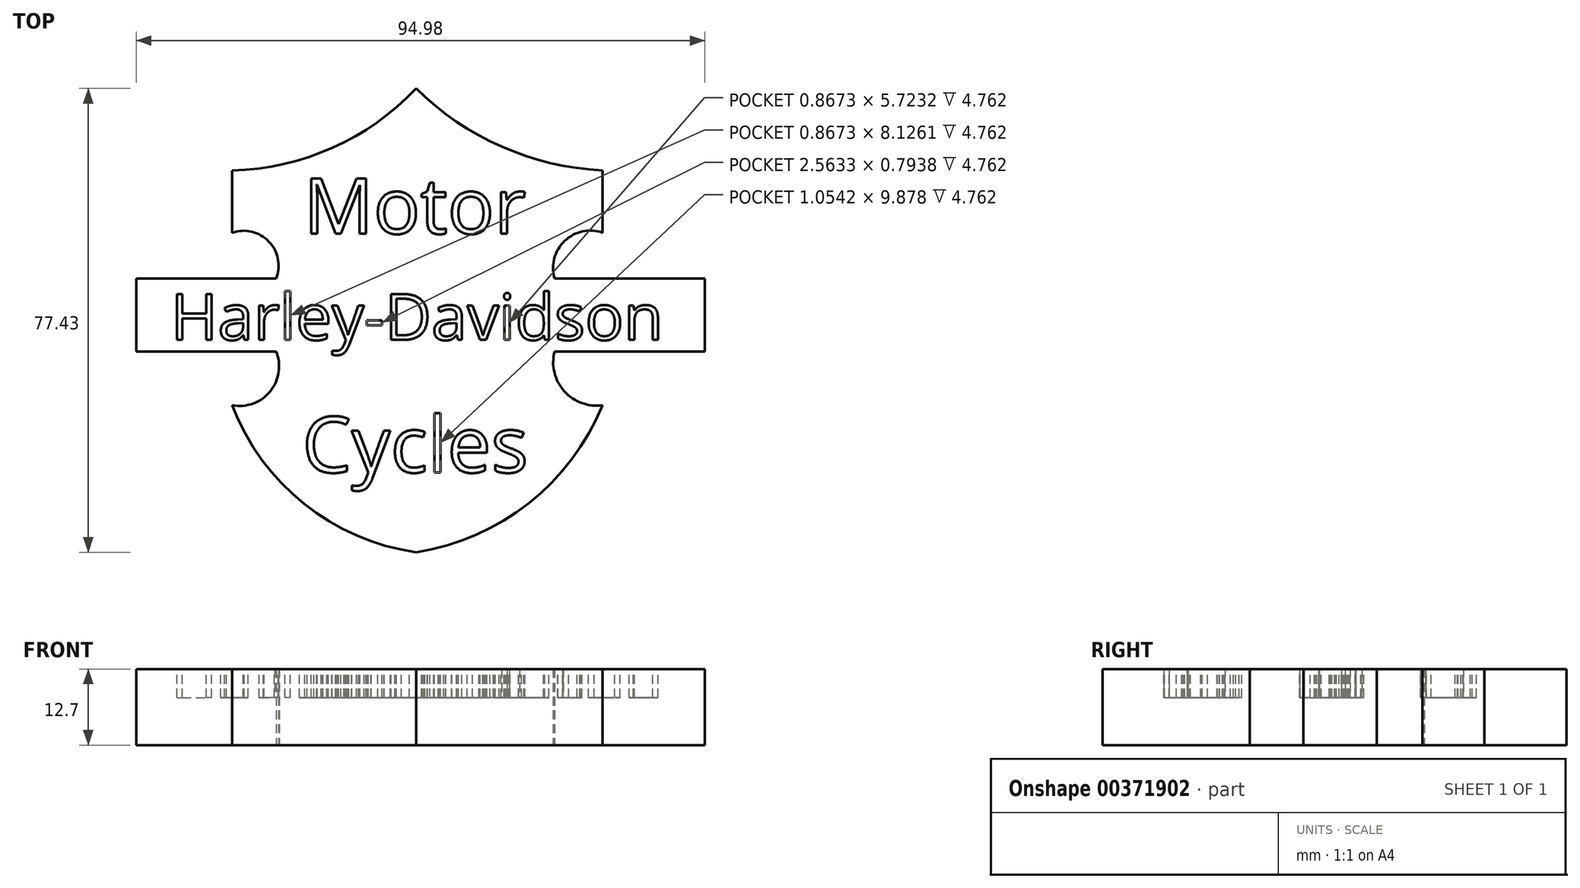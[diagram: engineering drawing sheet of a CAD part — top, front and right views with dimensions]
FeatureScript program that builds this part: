
annotation { "Feature Type Name" : "Feature", "Feature Type Description" : "" }
export const myFeature = defineFeature(function(context is Context, id is Id, definition is map)
    precondition{}
    {
        {
            var Q0;
            Q0=qCreatedBy(makeId("Top.planeOp"),FACE);
            var sketch = newSketch(context, id + "F0", { "sketchPlane" : qUnion([Q0])});
            skArc(sketch, "E0", {"start": v(-30.69, 35.65) * mm, "mid": v(-13.97, 39.42) * mm, "end": v(0, 49.34) * mm});
            skArc(sketch, "E1", {"start": v(0, 49.34) * mm, "mid": v(14.32, 39.61) * mm, "end": v(31.16, 35.65) * mm});
            skLineSegment(sketch, "E2", {"start": v(-30.69, 35.65) * mm, "end": v(-30.69, 25.26) * mm});
            skLineSegment(sketch, "E3", {"start": v(31.16, 35.65) * mm, "end": v(31.16, 25.26) * mm});
            skArc(sketch, "E4", {"start": v(31.16, 25.26) * mm, "mid": v(24.82, 23.9) * mm, "end": v(23.14, 17.63) * mm});
            skLineSegment(sketch, "E5", {"start": v(23.14, 17.63) * mm, "end": v(48.24, 17.63) * mm});
            skLineSegment(sketch, "E6", {"start": v(48.24, 17.63) * mm, "end": v(48.24, 5.43) * mm});
            skLineSegment(sketch, "E7", {"start": v(-46.74, 5.43) * mm, "end": v(-46.74, 17.63) * mm});
            skArc(sketch, "E8", {"start": v(23.14, 5.43) * mm, "mid": v(24.75, -1.2) * mm, "end": v(31.16, -3.54) * mm});
            skArc(sketch, "E9", {"start": v(-30.69, -3.54) * mm, "mid": v(-18.7, -20) * mm, "end": v(0, -28.1) * mm});
            skArc(sketch, "E10", {"start": v(0, -28.1) * mm, "mid": v(18.8, -19.9) * mm, "end": v(31.16, -3.54) * mm});
            skArc(sketch, "E11", {"start": v(-30.69, -3.54) * mm, "mid": v(-24.36, -1.24) * mm, "end": v(-23.35, 5.43) * mm});
            skArc(sketch, "E12", {"start": v(-23.35, 17.63) * mm, "mid": v(-24.58, 23.79) * mm, "end": v(-30.69, 25.26) * mm});
            skLineSegment(sketch, "E13", {"start": v(-23.35, 17.63) * mm, "end": v(-46.74, 17.63) * mm});
            skLineSegment(sketch, "E14", {"start": v(-46.74, 5.43) * mm, "end": v(-23.35, 5.43) * mm});
            skLineSegment(sketch, "E15", {"start": v(23.14, 5.43) * mm, "end": v(48.24, 5.43) * mm});
            skSolve(sketch);
        }
        {
            var Q0;
            Q0=makeQuery(id+"F0.imprint","IMPRINT",FACE,{"disambiguationData":[TD([[makeQuery(id+"F0.imprint","IMPRINT",EDGE,{"derivedFrom":sQuery(id+"F0.wireOp",EDGE,"E0")}),-1.0]])]});
            var Q1;
            Q1=makeQuery(id+"F0.imprint","IMPRINT",FACE,{"disambiguationData":[TD([[makeQuery(id+"F0.imprint","IMPRINT",EDGE,{"derivedFrom":sQuery(id+"F0.wireOp",EDGE,"38d3032f-426a-4906-8454-d546ac383862.sketch_text.stroke-173")}),1.0]])]});
            var Q2;
            Q2=makeQuery(id+"F0.imprint","IMPRINT",FACE,{"disambiguationData":[TD([[makeQuery(id+"F0.imprint","IMPRINT",EDGE,{"derivedFrom":sQuery(id+"F0.wireOp",EDGE,"38d3032f-426a-4906-8454-d546ac383862.sketch_text.stroke-216")}),1.0]])]});
            var Q3;
            Q3=makeQuery(id+"F0.imprint","IMPRINT",FACE,{"disambiguationData":[TD([[makeQuery(id+"F0.imprint","IMPRINT",EDGE,{"derivedFrom":sQuery(id+"F0.wireOp",EDGE,"fb05afc6-232a-44e7-864e-b6d0d33b0555.sketch_text.stroke-63")}),1.0]])]});
            var Q4;
            Q4=makeQuery(id+"F0.imprint","IMPRINT",FACE,{"disambiguationData":[TD([[makeQuery(id+"F0.imprint","IMPRINT",EDGE,{"derivedFrom":sQuery(id+"F0.wireOp",EDGE,"fb05afc6-232a-44e7-864e-b6d0d33b0555.sketch_text.stroke-27")}),1.0]])]});
            var Q5;
            Q5=makeQuery(id+"F0.imprint","IMPRINT",FACE,{"disambiguationData":[TD([[makeQuery(id+"F0.imprint","IMPRINT",EDGE,{"derivedFrom":sQuery(id+"F0.wireOp",EDGE,"38d3032f-426a-4906-8454-d546ac383862.sketch_text.stroke-102")}),1.0]])]});
            var Q6;
            Q6=makeQuery(id+"F0.imprint","IMPRINT",FACE,{"disambiguationData":[TD([[makeQuery(id+"F0.imprint","IMPRINT",EDGE,{"derivedFrom":sQuery(id+"F0.wireOp",EDGE,"38d3032f-426a-4906-8454-d546ac383862.sketch_text.stroke-31")}),1.0]])]});
            var Q7;
            Q7=makeQuery(id+"F0.imprint","IMPRINT",FACE,{"disambiguationData":[TD([[makeQuery(id+"F0.imprint","IMPRINT",EDGE,{"derivedFrom":sQuery(id+"F0.wireOp",EDGE,"38d3032f-426a-4906-8454-d546ac383862.sketch_text.stroke-70")}),1.0]])]});
            var Q8;
            Q8=makeQuery(id+"F0.imprint","IMPRINT",FACE,{"disambiguationData":[TD([[makeQuery(id+"F0.imprint","IMPRINT",EDGE,{"derivedFrom":sQuery(id+"F0.wireOp",EDGE,"38d3032f-426a-4906-8454-d546ac383862.sketch_text.stroke-128")}),1.0]])]});
            var Q9;
            Q9=makeQuery(id+"F0.imprint","IMPRINT",FACE,{"disambiguationData":[TD([[makeQuery(id+"F0.imprint","IMPRINT",EDGE,{"derivedFrom":sQuery(id+"F0.wireOp",EDGE,"3be71efd-9f48-4feb-90e3-6328f18f5e6b.sketch_text.stroke-64")}),1.0]])]});
            extrude(context, id + "F1", {"entities" : qUnion([Q0, Q1, Q2, Q3, Q4, Q5, Q6, Q7, Q8, Q9]), "depth" : 12.7 * mm});
        }
        {
            var Q0;
            Q0=makeQuery(id+"F1.opExtrude","CAP_FACE",FACE,{"disambiguationData":[OSD([sQuery(id+"F0.wireOp",EDGE,"E0"),sQuery(id+"F0.wireOp",EDGE,"E1"),sQuery(id+"F0.wireOp",EDGE,"E2"),sQuery(id+"F0.wireOp",EDGE,"E3"),sQuery(id+"F0.wireOp",EDGE,"E4"),sQuery(id+"F0.wireOp",EDGE,"E5"),sQuery(id+"F0.wireOp",EDGE,"E6"),sQuery(id+"F0.wireOp",EDGE,"E7"),sQuery(id+"F0.wireOp",EDGE,"E8"),sQuery(id+"F0.wireOp",EDGE,"E9"),sQuery(id+"F0.wireOp",EDGE,"E10"),sQuery(id+"F0.wireOp",EDGE,"E11"),sQuery(id+"F0.wireOp",EDGE,"E12"),sQuery(id+"F0.wireOp",EDGE,"E13"),sQuery(id+"F0.wireOp",EDGE,"E14"),sQuery(id+"F0.wireOp",EDGE,"E15")])],"isStart":false});
            var sketch = newSketch(context, id + "F2", { "sketchPlane" : qUnion([Q0])});
            skText(sketch, "E16", { "text": "Harley-Davidson", "fontName": "OpenSans-Regular.ttf"});
            skText(sketch, "E17", { "text": "Cycles", "fontName": "OpenSans-Regular.ttf"});
            skText(sketch, "E18", { "text": "Motor", "fontName": "OpenSans-Regular.ttf"});
            const initialGuessF2  = {"E16": [-0.04098, 0.00736, 1, 0, 0.0077], "E17": [-0.019, -0.01476, 1, 0, 0.00936], "E18": [-0.01876, 0.0251, 1, 0, 0.0093]};
            skSetInitialGuess(sketch, initialGuessF2);
            skSolve(sketch);
        }
        {
            var Q0;
            Q0=makeQuery(id+"F2.imprint","IMPRINT",FACE,{"disambiguationData":[TD([[makeQuery(id+"F2.imprint","IMPRINT",EDGE,{"derivedFrom":sQuery(id+"F2.wireOp",EDGE,"E16.sketch_text.stroke-224")}),-1.0]])]});
            var Q1;
            Q1=makeQuery(id+"F2.imprint","IMPRINT",FACE,{"disambiguationData":[TD([[makeQuery(id+"F2.imprint","IMPRINT",EDGE,{"derivedFrom":sQuery(id+"F2.wireOp",EDGE,"E16.sketch_text.stroke-207")}),-1.0]])]});
            var Q2;
            Q2=makeQuery(id+"F2.imprint","IMPRINT",FACE,{"disambiguationData":[TD([[makeQuery(id+"F2.imprint","IMPRINT",EDGE,{"derivedFrom":sQuery(id+"F2.wireOp",EDGE,"E16.sketch_text.stroke-182")}),-1.0]])]});
            var Q3;
            Q3=makeQuery(id+"F2.imprint","IMPRINT",FACE,{"disambiguationData":[TD([[makeQuery(id+"F2.imprint","IMPRINT",EDGE,{"derivedFrom":sQuery(id+"F2.wireOp",EDGE,"E16.sketch_text.stroke-158")}),-1.0]])]});
            var Q4;
            Q4=makeQuery(id+"F2.imprint","IMPRINT",FACE,{"disambiguationData":[TD([[makeQuery(id+"F2.imprint","IMPRINT",EDGE,{"derivedFrom":sQuery(id+"F2.wireOp",EDGE,"E16.sketch_text.stroke-146")}),-1.0]])]});
            var Q5;
            Q5=makeQuery(id+"F2.imprint","IMPRINT",FACE,{"disambiguationData":[TD([[makeQuery(id+"F2.imprint","IMPRINT",EDGE,{"derivedFrom":sQuery(id+"F2.wireOp",EDGE,"E16.sketch_text.stroke-150")}),-1.0]])]});
            var Q6;
            Q6=makeQuery(id+"F2.imprint","IMPRINT",FACE,{"disambiguationData":[TD([[makeQuery(id+"F2.imprint","IMPRINT",EDGE,{"derivedFrom":sQuery(id+"F2.wireOp",EDGE,"E16.sketch_text.stroke-136")}),-1.0]])]});
            var Q7;
            Q7=makeQuery(id+"F2.imprint","IMPRINT",FACE,{"disambiguationData":[TD([[makeQuery(id+"F2.imprint","IMPRINT",EDGE,{"derivedFrom":sQuery(id+"F2.wireOp",EDGE,"E16.sketch_text.stroke-109")}),-1.0]])]});
            var Q8;
            Q8=makeQuery(id+"F2.imprint","IMPRINT",FACE,{"disambiguationData":[TD([[makeQuery(id+"F2.imprint","IMPRINT",EDGE,{"derivedFrom":sQuery(id+"F2.wireOp",EDGE,"E16.sketch_text.stroke-95")}),-1.0]])]});
            var Q9;
            Q9=makeQuery(id+"F2.imprint","IMPRINT",FACE,{"disambiguationData":[TD([[makeQuery(id+"F2.imprint","IMPRINT",EDGE,{"derivedFrom":sQuery(id+"F2.wireOp",EDGE,"E16.sketch_text.stroke-91")}),-1.0]])]});
            var Q10;
            Q10=makeQuery(id+"F2.imprint","IMPRINT",FACE,{"disambiguationData":[TD([[makeQuery(id+"F2.imprint","IMPRINT",EDGE,{"derivedFrom":sQuery(id+"F2.wireOp",EDGE,"E16.sketch_text.stroke-75")}),-1.0]])]});
            var Q11;
            Q11=makeQuery(id+"F2.imprint","IMPRINT",FACE,{"disambiguationData":[TD([[makeQuery(id+"F2.imprint","IMPRINT",EDGE,{"derivedFrom":sQuery(id+"F2.wireOp",EDGE,"E16.sketch_text.stroke-56")}),-1.0]])]});
            var Q12;
            Q12=makeQuery(id+"F2.imprint","IMPRINT",FACE,{"disambiguationData":[TD([[makeQuery(id+"F2.imprint","IMPRINT",EDGE,{"derivedFrom":sQuery(id+"F2.wireOp",EDGE,"E16.sketch_text.stroke-52")}),-1.0]])]});
            var Q13;
            Q13=makeQuery(id+"F2.imprint","IMPRINT",FACE,{"disambiguationData":[TD([[makeQuery(id+"F2.imprint","IMPRINT",EDGE,{"derivedFrom":sQuery(id+"F2.wireOp",EDGE,"E16.sketch_text.stroke-39")}),-1.0]])]});
            var Q14;
            Q14=makeQuery(id+"F2.imprint","IMPRINT",FACE,{"disambiguationData":[TD([[makeQuery(id+"F2.imprint","IMPRINT",EDGE,{"derivedFrom":sQuery(id+"F2.wireOp",EDGE,"E16.sketch_text.stroke-12")}),-1.0]])]});
            var Q15;
            Q15=makeQuery(id+"F2.imprint","IMPRINT",FACE,{"disambiguationData":[TD([[makeQuery(id+"F2.imprint","IMPRINT",EDGE,{"derivedFrom":sQuery(id+"F2.wireOp",EDGE,"E16.sketch_text.stroke-0")}),-1.0]])]});
            var Q16;
            Q16=makeQuery(id+"F2.imprint","IMPRINT",FACE,{"disambiguationData":[TD([[makeQuery(id+"F2.imprint","IMPRINT",EDGE,{"derivedFrom":sQuery(id+"F2.wireOp",EDGE,"E18.sketch_text.stroke-0")}),-1.0]])]});
            var Q17;
            Q17=makeQuery(id+"F2.imprint","IMPRINT",FACE,{"disambiguationData":[TD([[makeQuery(id+"F2.imprint","IMPRINT",EDGE,{"derivedFrom":sQuery(id+"F2.wireOp",EDGE,"E18.sketch_text.stroke-18")}),-1.0]])]});
            var Q18;
            Q18=makeQuery(id+"F2.imprint","IMPRINT",FACE,{"disambiguationData":[TD([[makeQuery(id+"F2.imprint","IMPRINT",EDGE,{"derivedFrom":sQuery(id+"F2.wireOp",EDGE,"E18.sketch_text.stroke-35")}),-1.0]])]});
            var Q19;
            Q19=makeQuery(id+"F2.imprint","IMPRINT",FACE,{"disambiguationData":[TD([[makeQuery(id+"F2.imprint","IMPRINT",EDGE,{"derivedFrom":sQuery(id+"F2.wireOp",EDGE,"E18.sketch_text.stroke-54")}),-1.0]])]});
            var Q20;
            Q20=makeQuery(id+"F2.imprint","IMPRINT",FACE,{"disambiguationData":[TD([[makeQuery(id+"F2.imprint","IMPRINT",EDGE,{"derivedFrom":sQuery(id+"F2.wireOp",EDGE,"E18.sketch_text.stroke-71")}),-1.0]])]});
            var Q21;
            Q21=makeQuery(id+"F2.imprint","IMPRINT",FACE,{"disambiguationData":[TD([[makeQuery(id+"F2.imprint","IMPRINT",EDGE,{"derivedFrom":sQuery(id+"F2.wireOp",EDGE,"E17.sketch_text.stroke-0")}),-1.0]])]});
            var Q22;
            Q22=makeQuery(id+"F2.imprint","IMPRINT",FACE,{"disambiguationData":[TD([[makeQuery(id+"F2.imprint","IMPRINT",EDGE,{"derivedFrom":sQuery(id+"F2.wireOp",EDGE,"E17.sketch_text.stroke-15")}),-1.0]])]});
            var Q23;
            Q23=makeQuery(id+"F2.imprint","IMPRINT",FACE,{"disambiguationData":[TD([[makeQuery(id+"F2.imprint","IMPRINT",EDGE,{"derivedFrom":sQuery(id+"F2.wireOp",EDGE,"E17.sketch_text.stroke-31")}),-1.0]])]});
            var Q24;
            Q24=makeQuery(id+"F2.imprint","IMPRINT",FACE,{"disambiguationData":[TD([[makeQuery(id+"F2.imprint","IMPRINT",EDGE,{"derivedFrom":sQuery(id+"F2.wireOp",EDGE,"E17.sketch_text.stroke-46")}),-1.0]])]});
            var Q25;
            Q25=makeQuery(id+"F2.imprint","IMPRINT",FACE,{"disambiguationData":[TD([[makeQuery(id+"F2.imprint","IMPRINT",EDGE,{"derivedFrom":sQuery(id+"F2.wireOp",EDGE,"E17.sketch_text.stroke-50")}),-1.0]])]});
            var Q26;
            Q26=makeQuery(id+"F2.imprint","IMPRINT",FACE,{"disambiguationData":[TD([[makeQuery(id+"F2.imprint","IMPRINT",EDGE,{"derivedFrom":sQuery(id+"F2.wireOp",EDGE,"E17.sketch_text.stroke-69")}),-1.0]])]});
            extrude(context, id + "F3", {"entities" : qUnion([Q0, Q1, Q2, Q3, Q4, Q5, Q6, Q7, Q8, Q9, Q10, Q11, Q12, Q13, Q14, Q15, Q16, Q17, Q18, Q19, Q20, Q21, Q22, Q23, Q24, Q25, Q26]), "operationType" : NewBodyOperationType.REMOVE, "oppositeDirection" : true, "depth" : 4.76 * mm});
        }
    });
